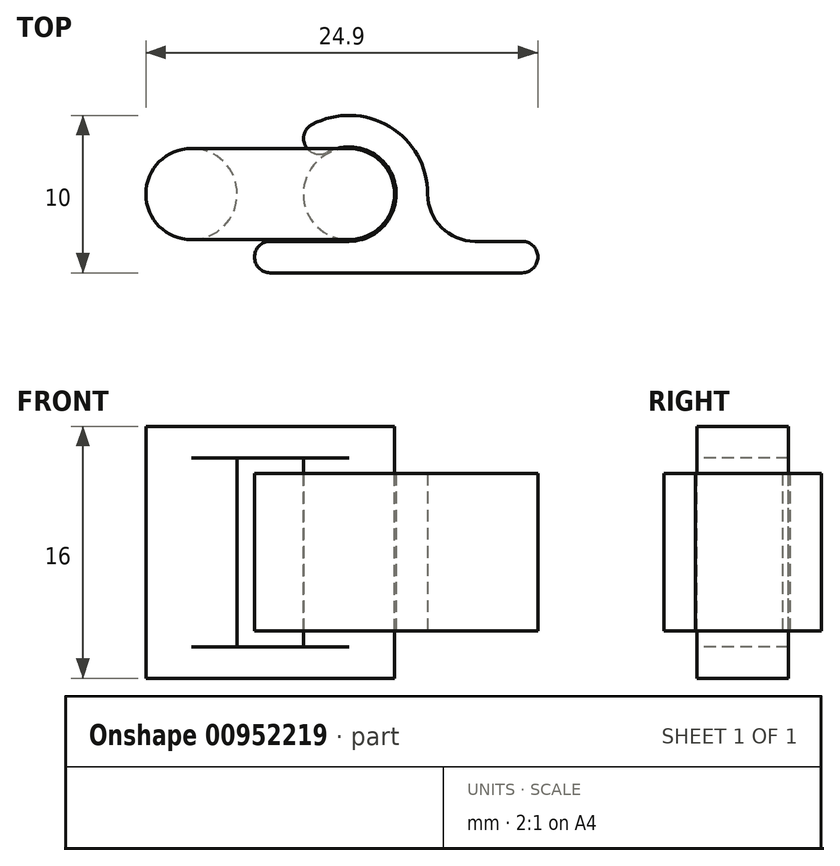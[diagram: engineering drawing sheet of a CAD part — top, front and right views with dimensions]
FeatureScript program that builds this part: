
annotation { "Feature Type Name" : "Feature", "Feature Type Description" : "" }
export const myFeature = defineFeature(function(context is Context, id is Id, definition is map)
    precondition{}
    {
        {
            var Q0;
            Q0=qCreatedBy(makeId("Top.planeOp"),FACE);
            var sketch = newSketch(context, id + "F0", { "sketchPlane" : qUnion([Q0])});
            skArc(sketch, "E0", {"start": v(0, -3) * mm, "mid": v(2.91, 0.73) * mm, "end": v(-1.4, 2.65) * mm});
            skLineSegment(sketch, "E1", {"start": v(0, 0) * mm, "end": v(-2.03, 2.21) * mm, "construction": true});
            skLineSegment(sketch, "E2", {"start": v(0, 0) * mm, "end": v(0, -3) * mm, "construction": true});
            skLineSegment(sketch, "E3", {"start": v(0, -3) * mm, "end": v(-5, -3) * mm});
            skArc(sketch, "E4.0", {"start": v(5, 0) * mm, "mid": v(2.57, 4.29) * mm, "end": v(-2.35, 4.41) * mm});
            skLineSegment(sketch, "E4.1", {"start": v(0, -5) * mm, "end": v(-5, -5) * mm});
            skLineSegment(sketch, "E5", {"start": v(-2.62, 2.86) * mm, "end": v(-2.62, 2.86) * mm});
            skLineSegment(sketch, "E6", {"start": v(-6, -4) * mm, "end": v(-6, -4) * mm});
            skLineSegment(sketch, "E7", {"start": v(0, -5) * mm, "end": v(11, -5) * mm});
            skLineSegment(sketch, "E8", {"start": v(12, -4) * mm, "end": v(12, -4) * mm});
            skLineSegment(sketch, "E9", {"start": v(11, -3) * mm, "end": v(8, -3) * mm});
            skPoint(sketch, "E10", {"position": v(5, 0) * mm});
            skLineSegment(sketch, "E11", {"start": v(5, 0) * mm, "end": v(5, 0) * mm});
            skPoint(sketch, "E12.visualSharp", {"position": v(5, -3) * mm});
            skArc(sketch, "E12.filletArc", {"start": v(5, 0) * mm, "mid": v(5.88, -2.12) * mm, "end": v(8, -3) * mm});
            skPoint(sketch, "E13.visualSharp", {"position": v(-2.03, 2.21) * mm});
            skArc(sketch, "E13.filletArc", {"start": v(-2.62, 2.86) * mm, "mid": v(-2.05, 2.55) * mm, "end": v(-1.4, 2.65) * mm});
            skPoint(sketch, "E14.visualSharp", {"position": v(-3.38, 3.69) * mm});
            skArc(sketch, "E14.filletArc", {"start": v(-2.35, 4.41) * mm, "mid": v(-2.86, 3.7) * mm, "end": v(-2.62, 2.86) * mm});
            skPoint(sketch, "E15.visualSharp", {"position": v(-6, -3) * mm});
            skArc(sketch, "E15.filletArc", {"start": v(-5, -3) * mm, "mid": v(-5.7, -3.3) * mm, "end": v(-6, -4) * mm});
            skPoint(sketch, "E16.visualSharp", {"position": v(-6, -5) * mm});
            skArc(sketch, "E16.filletArc", {"start": v(-6, -4) * mm, "mid": v(-5.7, -4.7) * mm, "end": v(-5, -5) * mm});
            skPoint(sketch, "E17.visualSharp", {"position": v(12, -3) * mm});
            skArc(sketch, "E17.filletArc", {"start": v(12, -4) * mm, "mid": v(11.7, -3.3) * mm, "end": v(11, -3) * mm});
            skPoint(sketch, "E18.visualSharp", {"position": v(12, -5) * mm});
            skArc(sketch, "E18.filletArc", {"start": v(11, -5) * mm, "mid": v(11.7, -4.7) * mm, "end": v(12, -4) * mm});
            skSolve(sketch);
        }
        {
            var Q0;
            Q0 = qSketchRegion(id + "F0", true);
            extrude(context, id + "F1", {"entities" : qUnion([Q0]), "depth" : 10 * mm, "offsetDistance" : 25.4 * mm});
        }
        {
            var Q0;
            Q0=makeQuery(id+"F1.opExtrude","CAP_FACE",FACE,{"disambiguationData":[OSD([sQuery(id+"F0.wireOp",EDGE,"E0"),sQuery(id+"F0.wireOp",EDGE,"E3"),sQuery(id+"F0.wireOp",EDGE,"E4.0"),sQuery(id+"F0.wireOp",EDGE,"E4.1"),sQuery(id+"F0.wireOp",EDGE,"E7"),sQuery(id+"F0.wireOp",EDGE,"E9"),sQuery(id+"F0.wireOp",EDGE,"E12.filletArc"),sQuery(id+"F0.wireOp",EDGE,"E13.filletArc"),sQuery(id+"F0.wireOp",EDGE,"E14.filletArc"),sQuery(id+"F0.wireOp",EDGE,"E15.filletArc"),sQuery(id+"F0.wireOp",EDGE,"E16.filletArc"),sQuery(id+"F0.wireOp",EDGE,"E17.filletArc"),sQuery(id+"F0.wireOp",EDGE,"E18.filletArc")])],"isStart":false});
            var sketch = newSketch(context, id + "F2", { "sketchPlane" : qUnion([Q0])});
            skCircle(sketch, "E19", {"center": v(0, 0) * mm, "radius": 2.9 * mm});
            skLineSegment(sketch, "E20", {"start": v(0, 0) * mm, "end": v(-10, 0) * mm, "construction": true});
            skCircle(sketch, "E21", {"center": v(-10, 0) * mm, "radius": 2.9 * mm});
            skSolve(sketch);
        }
        {
            var Q0;
            Q0 = qSketchRegion(id + "F2", true);
            extrude(context, id + "F3", {"entities" : qUnion([Q0]), "oppositeDirection" : true, "depth" : 11 * mm, "offsetDistance" : 25.4 * mm, "hasSecondDirection" : true, "secondDirectionOppositeDirection" : false, "secondDirectionDepth" : 1 * mm});
        }
        {
            var Q0;
            Q0=makeQuery(id+"F3.opExtrude","CAP_FACE",FACE,{"disambiguationData":[OSD([sQuery(id+"F2.wireOp",EDGE,"E19")])],"isStart":false});
            var sketch = newSketch(context, id + "F4", { "sketchPlane" : qUnion([Q0])});
            skArc(sketch, "E22", {"start": v(0, -2.9) * mm, "mid": v(2.9, 0) * mm, "end": v(0, 2.9) * mm});
            skArc(sketch, "E23", {"start": v(-10, 2.9) * mm, "mid": v(-12.9, 0) * mm, "end": v(-10, -2.9) * mm});
            skLineSegment(sketch, "E24", {"start": v(0, 2.9) * mm, "end": v(-10, 2.9) * mm});
            skPoint(sketch, "E25.end.orphan", {"position": v(0, -2.9) * mm});
            skLineSegment(sketch, "E26", {"start": v(0, -2.9) * mm, "end": v(-10, -2.9) * mm});
            skSolve(sketch);
        }
        {
            var Q0;
            Q0 = qSketchRegion(id + "F4", true);
            extrude(context, id + "F5", {"entities" : qUnion([Q0]), "operationType" : NewBodyOperationType.ADD, "depth" : 2 * mm, "offsetDistance" : 25.4 * mm});
        }
        {
            var Q0;
            Q0=makeQuery(id+"F3.opExtrude","CAP_FACE",FACE,{"disambiguationData":[OSD([sQuery(id+"F2.wireOp",EDGE,"E21")])],"isStart":true});
            var sketch = newSketch(context, id + "F6", { "sketchPlane" : qUnion([Q0])});
            skArc(sketch, "E27", {"start": v(0, -2.9) * mm, "mid": v(2.9, 0) * mm, "end": v(0, 2.9) * mm});
            skArc(sketch, "E28", {"start": v(-10, 2.9) * mm, "mid": v(-12.9, 0) * mm, "end": v(-10, -2.9) * mm});
            skLineSegment(sketch, "E29", {"start": v(-10, 2.9) * mm, "end": v(0, 2.9) * mm});
            skLineSegment(sketch, "E30", {"start": v(0, -2.9) * mm, "end": v(-10, -2.9) * mm});
            skSolve(sketch);
        }
        {
            var Q0;
            Q0 = qSketchRegion(id + "F6", true);
            extrude(context, id + "F7", {"entities" : qUnion([Q0]), "operationType" : NewBodyOperationType.ADD, "depth" : 2 * mm, "offsetDistance" : 25.4 * mm});
        }
    });
